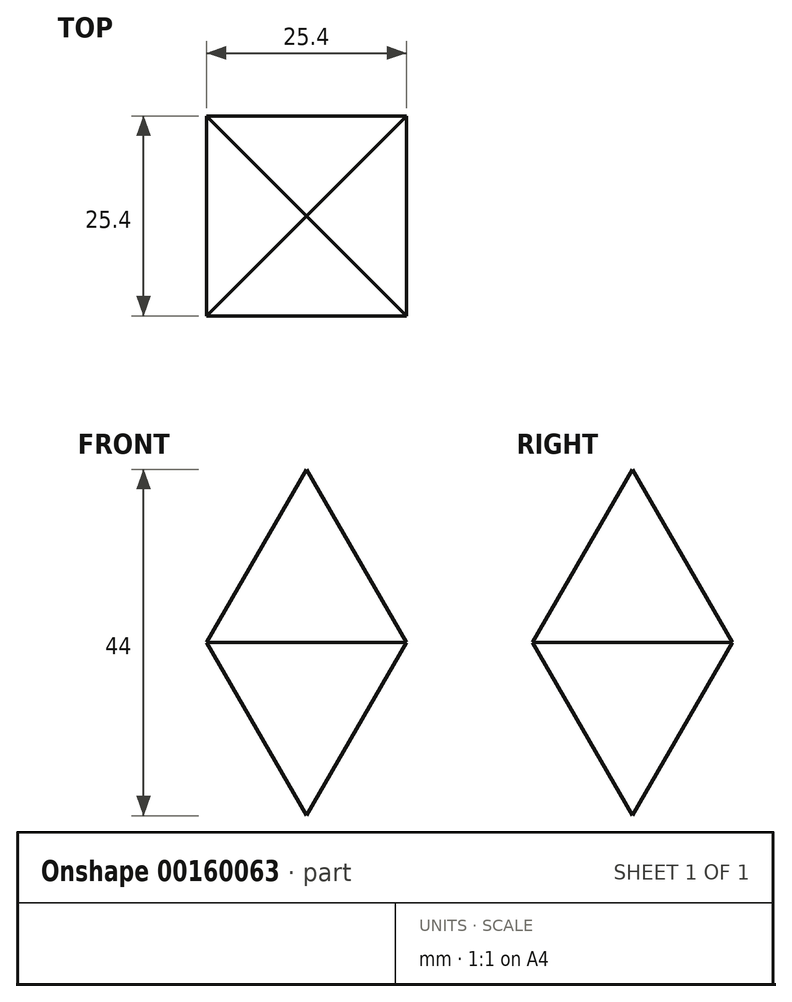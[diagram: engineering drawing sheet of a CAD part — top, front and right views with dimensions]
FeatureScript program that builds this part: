
annotation { "Feature Type Name" : "Feature", "Feature Type Description" : "" }
export const myFeature = defineFeature(function(context is Context, id is Id, definition is map)
    precondition{}
    {
        {
            var Q0;
            Q0=qCreatedBy(makeId("Top.planeOp"),FACE);
            var sketch = newSketch(context, id + "F0", { "sketchPlane" : qUnion([Q0])});
            skLineSegment(sketch, "E0.bottom", {"start": v(12.7, 12.7) * mm, "end": v(-12.7, 12.7) * mm});
            skLineSegment(sketch, "E0.top", {"start": v(12.7, -12.7) * mm, "end": v(-12.7, -12.7) * mm});
            skLineSegment(sketch, "E0.left", {"start": v(12.7, 12.7) * mm, "end": v(12.7, -12.7) * mm});
            skLineSegment(sketch, "E0.right", {"start": v(-12.7, 12.7) * mm, "end": v(-12.7, -12.7) * mm});
            skPoint(sketch, "E0.middle", {"position": v(0, 0) * mm});
            skSolve(sketch);
        }
        {
            var Q0;
            Q0=makeQuery(id+"F0.imprint","IMPRINT",FACE,{"disambiguationData":[TD([[makeQuery(id+"F0.imprint","IMPRINT",EDGE,{"derivedFrom":sQuery(id+"F0.wireOp",EDGE,"E0.bottom")}),1.0]])]});
            extrude(context, id + "F1", {"entities" : qUnion([Q0]), "oppositeDirection" : true, "depth" : 25.4 * mm, "hasDraft" : true, "draftAngle" : 30 * degree, "draftPullDirection" : true, "hasSecondDirection" : true, "secondDirectionOppositeDirection" : false, "secondDirectionDepth" : 25.4 * mm, "hasSecondDirectionDraft" : true, "secondDirectionDraftAngle" : 30 * degree, "secondDirectionDraftPullDirection" : true});
        }
    });
